# Revit family: Specialty Equipment_Coat Hook_Metlam_ML2162af1e8ca-08bd-46d0-a06a-f0845abb1084
name_source: partatom
category: Specialty Equipment
revit_build: Autodesk Revit 2014 (Build: 20130308_1515(x64)
units: mm (PartAtom-declared; Revit-internal decimal feet)

## types (1)
- 76w x 76h x 83d
    Assembly Code = C1030200
    Description = Concealed Fix HD Coat Hook - SS Finish
    Manufacturer = Metlam
    Manufacturer_Overall Depth = 83 mm  [stored 0.27231 ft]
    Manufacturer_Overall Height = 76 mm  [stored 0.249344 ft]
    Manufacturer_Overall Width = 76 mm  [stored 0.249344 ft]
    Manufacturer_Spec Code = ML216
    Manufacturer_URL__Product Specific = http://www.metlam.com.au
    Material = z_Metlam_Metal_Stainless Steel Satin
    Model = ML216
    ModifiedIssue_ANZRS = 20150127 $
    Type Comments = ML216
    URL = www.metlam.com.au

note: [stored X ft] marks values corroborated as IEEE doubles in the binary element streams (Revit-internal decimal feet)

## geometry (parser evidence)
native form markers: Sweep x2
no freeform markers — native parametric forms only
